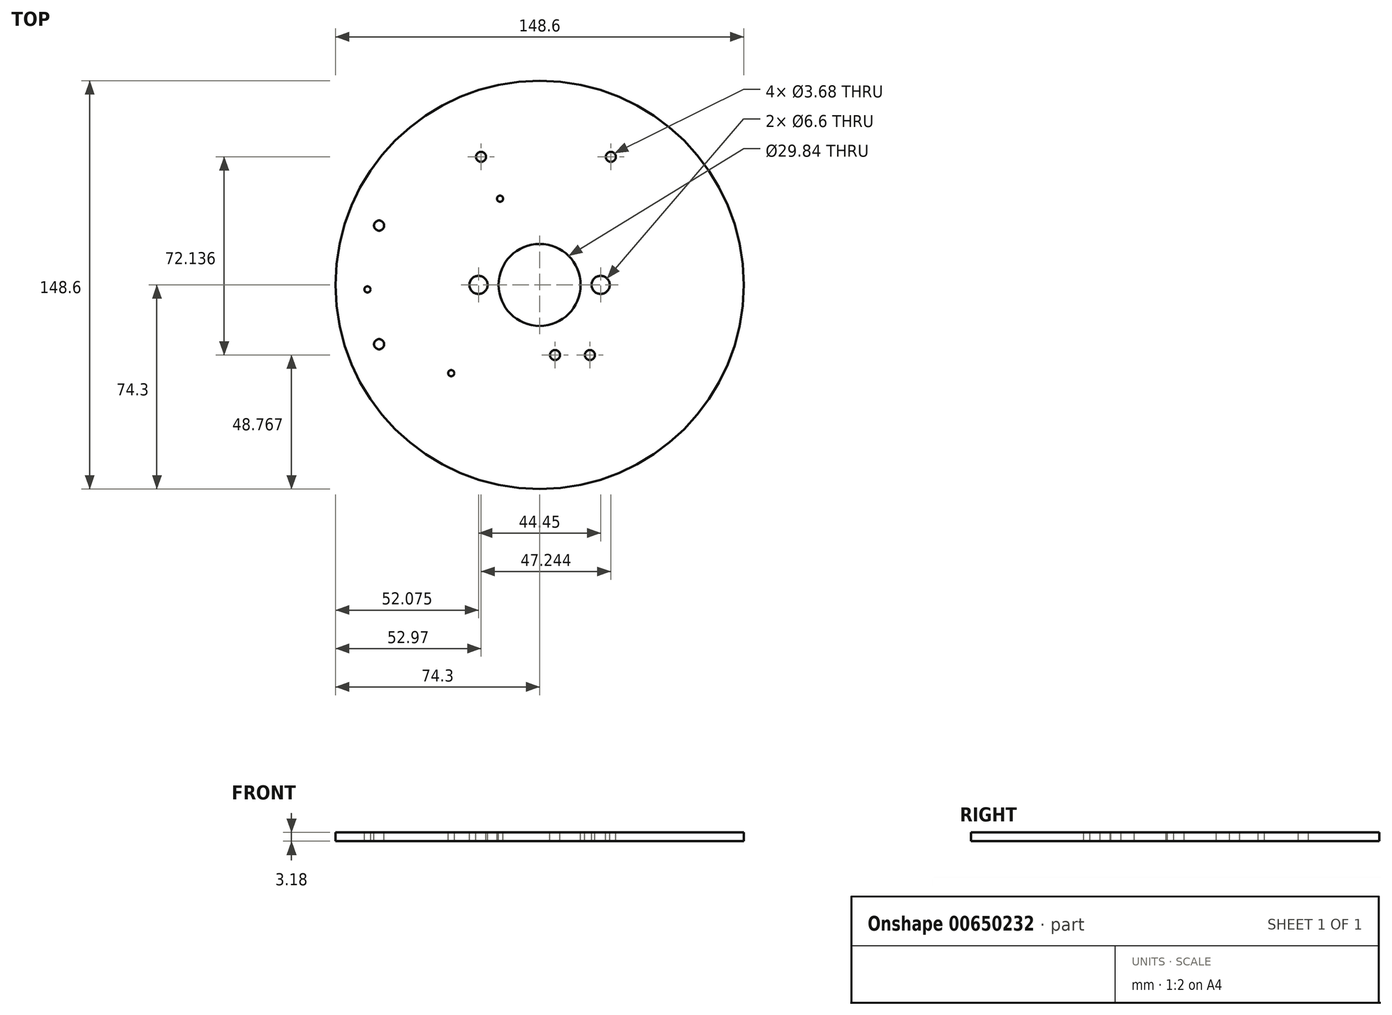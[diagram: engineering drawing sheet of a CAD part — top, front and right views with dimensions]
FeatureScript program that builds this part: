
annotation { "Feature Type Name" : "Feature", "Feature Type Description" : "" }
export const myFeature = defineFeature(function(context is Context, id is Id, definition is map)
    precondition{}
    {
        {
            var Q0;
            Q0=qCreatedBy(makeId("Top.planeOp"),FACE);
            var sketch = newSketch(context, id + "F0", { "sketchPlane" : qUnion([Q0])});
            skCircle(sketch, "E0", {"center": v(0, 0) * mm, "radius": 74.3 * mm});
            skSolve(sketch);
        }
        {
            var Q0;
            Q0=makeQuery(id+"F0.imprint","IMPRINT",FACE,{"disambiguationData":[TD([[makeQuery(id+"F0.imprint","IMPRINT",EDGE,{"derivedFrom":sQuery(id+"F0.wireOp",EDGE,"E0")}),1.0]])]});
            extrude(context, id + "F1", {"entities" : qUnion([Q0]), "depth" : 3.17 * mm, "offsetDistance" : 25.4 * mm});
        }
        {
            var Q0;
            Q0=makeQuery(id+"F1.opExtrude","CAP_FACE",FACE,{"disambiguationData":[OSD([sQuery(id+"F0.wireOp",EDGE,"E0")])],"isStart":false});
            var sketch = newSketch(context, id + "F2", { "sketchPlane" : qUnion([Q0])});
            skCircle(sketch, "E1", {"center": v(-58.42, 21.59) * mm, "radius": 1.85 * mm});
            skLineSegment(sketch, "E2", {"start": v(0, 0) * mm, "end": v(-74.3, 0) * mm, "construction": true});
            skLineSegment(sketch, "E3", {"start": v(-58.42, 21.59) * mm, "end": v(-58.42, 0) * mm});
            skCircle(sketch, "E4.MirrorC", {"center": v(-58.42, -21.6) * mm, "radius": 1.85 * mm});
            skSolve(sketch);
        }
        {
            var Q0;
            Q0 = qSketchRegion(id + "F2", true);
            extrude(context, id + "F3", {"entities" : qUnion([Q0]), "operationType" : NewBodyOperationType.REMOVE, "endBound" : BoundingType.THROUGH_ALL, "oppositeDirection" : true, "depth" : 25.4 * mm, "offsetDistance" : 25.4 * mm});
        }
        {
            var Q0;
            Q0=makeQuery(id+"F1.opExtrude","CAP_FACE",FACE,{"disambiguationData":[OSD([sQuery(id+"F0.wireOp",EDGE,"E0")])],"isStart":false});
            var sketch = newSketch(context, id + "F4", { "sketchPlane" : qUnion([Q0])});
            skCircle(sketch, "E5", {"center": v(0, 0) * mm, "radius": 14.92 * mm});
            skCircle(sketch, "E6", {"center": v(-22.23, 0) * mm, "radius": 3.3 * mm});
            skCircle(sketch, "E7.MirrorC", {"center": v(22.23, 0) * mm, "radius": 3.3 * mm});
            skSolve(sketch);
        }
        {
            var Q0;
            Q0 = qSketchRegion(id + "F4", true);
            extrude(context, id + "F5", {"entities" : qUnion([Q0]), "operationType" : NewBodyOperationType.REMOVE, "endBound" : BoundingType.THROUGH_ALL, "oppositeDirection" : true, "depth" : 25.4 * mm, "offsetDistance" : 25.4 * mm});
        }
        {
            var Q0;
            Q0=makeQuery(id+"F1.opExtrude","CAP_FACE",FACE,{"disambiguationData":[OSD([sQuery(id+"F0.wireOp",EDGE,"E0")])],"isStart":false});
            var sketch = newSketch(context, id + "F6", { "sketchPlane" : qUnion([Q0])});
            skCircle(sketch, "E8", {"center": v(-21.33, 46.6) * mm, "radius": 1.84 * mm});
            skCircle(sketch, "E9", {"center": v(25.91, 46.6) * mm, "radius": 1.84 * mm});
            skCircle(sketch, "E10", {"center": v(5.6, -25.53) * mm, "radius": 1.84 * mm});
            skCircle(sketch, "E11", {"center": v(18.3, -25.53) * mm, "radius": 1.84 * mm});
            skLineSegment(sketch, "E12", {"start": v(-21.33, 46.6) * mm, "end": v(25.91, 46.6) * mm, "construction": true});
            skLineSegment(sketch, "E13", {"start": v(5.6, -25.53) * mm, "end": v(18.3, -25.53) * mm, "construction": true});
            skSolve(sketch);
        }
        {
            var Q0;
            Q0 = qSketchRegion(id + "F6", true);
            extrude(context, id + "F7", {"entities" : qUnion([Q0]), "operationType" : NewBodyOperationType.REMOVE, "endBound" : BoundingType.THROUGH_ALL, "oppositeDirection" : true, "depth" : 25.4 * mm, "offsetDistance" : 25.4 * mm});
        }
        {
            var Q0;
            Q0=makeQuery(id+"F1.opExtrude","CAP_FACE",FACE,{"disambiguationData":[OSD([sQuery(id+"F0.wireOp",EDGE,"E0")])],"isStart":false});
            var sketch = newSketch(context, id + "F8", { "sketchPlane" : qUnion([Q0])});
            skLineSegment(sketch, "E14.bottom", {"start": v(-65.44, 35.18) * mm, "end": v(-10.32, 35.18) * mm, "construction": true});
            skLineSegment(sketch, "E14.top", {"start": v(-65.44, -35.18) * mm, "end": v(-10.32, -35.18) * mm, "construction": true});
            skLineSegment(sketch, "E14.left", {"start": v(-65.44, 35.18) * mm, "end": v(-65.44, -35.18) * mm, "construction": true});
            skLineSegment(sketch, "E14.right", {"start": v(-10.32, 35.18) * mm, "end": v(-10.32, -35.18) * mm, "construction": true});
            skCircle(sketch, "E15", {"center": v(-14.38, 31.37) * mm, "radius": 1.13 * mm});
            skCircle(sketch, "E16", {"center": v(-62.64, -1.65) * mm, "radius": 1.13 * mm});
            skCircle(sketch, "E17", {"center": v(-32.16, -32.13) * mm, "radius": 1.13 * mm});
            skSolve(sketch);
        }
        {
            var Q0;
            Q0 = qSketchRegion(id + "F8", true);
            extrude(context, id + "F9", {"entities" : qUnion([Q0]), "operationType" : NewBodyOperationType.REMOVE, "endBound" : BoundingType.THROUGH_ALL, "oppositeDirection" : true, "depth" : 25.4 * mm, "offsetDistance" : 25.4 * mm});
        }
    });
